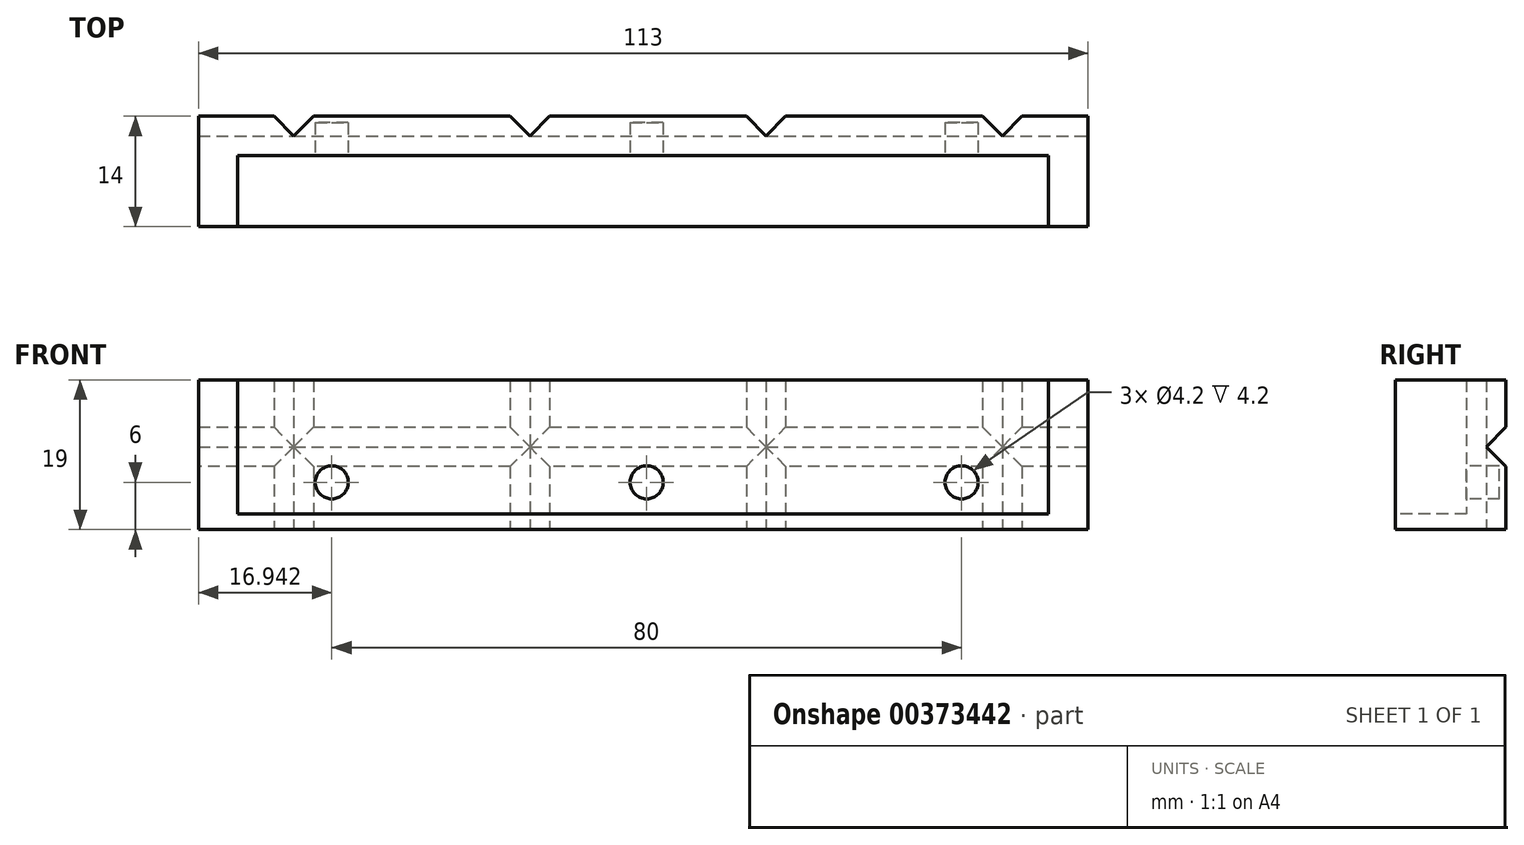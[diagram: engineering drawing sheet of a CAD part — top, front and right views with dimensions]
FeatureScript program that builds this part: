
annotation { "Feature Type Name" : "Feature", "Feature Type Description" : "" }
export const myFeature = defineFeature(function(context is Context, id is Id, definition is map)
    precondition{}
    {
        {
            var Q0;
            Q0=qCreatedBy(makeId("Top.planeOp"),FACE);
            var sketch = newSketch(context, id + "F0", { "sketchPlane" : qUnion([Q0])});
            skLineSegment(sketch, "E0.bottom", {"start": v(-52, -5) * mm, "end": v(51, -5) * mm});
            skLineSegment(sketch, "E0.top", {"start": v(-52, -14) * mm, "end": v(51, -14) * mm});
            skLineSegment(sketch, "E0.left", {"start": v(-52, -5) * mm, "end": v(-52, -14) * mm});
            skLineSegment(sketch, "E0.right", {"start": v(51, -5) * mm, "end": v(51, -14) * mm});
            skLineSegment(sketch, "E1", {"start": v(-57, -14) * mm, "end": v(-57, 0) * mm});
            skLineSegment(sketch, "E2", {"start": v(-57, 0) * mm, "end": v(56, 0) * mm});
            skLineSegment(sketch, "E3", {"start": v(56, 0) * mm, "end": v(56, -14) * mm});
            skLineSegment(sketch, "E4", {"start": v(-52, -14) * mm, "end": v(-57, -14) * mm});
            skLineSegment(sketch, "E5", {"start": v(56, -14) * mm, "end": v(51, -14) * mm});
            skLineSegment(sketch, "E6.direction1", {"start": v(-45, -9.6) * mm, "end": v(-15, -9.6) * mm, "construction": true});
            skLineSegment(sketch, "E7", {"start": v(-48.43, 1.04) * mm, "end": v(-44.9, -2.5) * mm});
            skLineSegment(sketch, "E8", {"start": v(-44.9, -2.5) * mm, "end": v(-41.36, 1.04) * mm});
            skLineSegment(sketch, "E9", {"start": v(-41.36, 1.04) * mm, "end": v(-48.43, 1.04) * mm});
            skLineSegment(sketch, "E10.1.0.0", {"start": v(-11.36, 1.04) * mm, "end": v(-18.43, 1.04) * mm});
            skLineSegment(sketch, "E10.1.0.1", {"start": v(-14.9, -2.5) * mm, "end": v(-11.36, 1.04) * mm});
            skLineSegment(sketch, "E10.1.0.2", {"start": v(-18.43, 1.04) * mm, "end": v(-14.9, -2.5) * mm});
            skLineSegment(sketch, "E10.2.0.0", {"start": v(18.64, 1.04) * mm, "end": v(11.57, 1.04) * mm});
            skLineSegment(sketch, "E10.2.0.1", {"start": v(15.1, -2.5) * mm, "end": v(18.64, 1.04) * mm});
            skLineSegment(sketch, "E10.2.0.2", {"start": v(11.57, 1.04) * mm, "end": v(15.1, -2.5) * mm});
            skLineSegment(sketch, "E10.3.0.0", {"start": v(48.64, 1.04) * mm, "end": v(41.57, 1.04) * mm});
            skLineSegment(sketch, "E10.3.0.1", {"start": v(45.1, -2.5) * mm, "end": v(48.64, 1.04) * mm});
            skLineSegment(sketch, "E10.3.0.2", {"start": v(41.57, 1.04) * mm, "end": v(45.1, -2.5) * mm});
            skLineSegment(sketch, "E10.direction1", {"start": v(-48.43, 1.04) * mm, "end": v(-18.43, 1.04) * mm, "construction": true});
            skSolve(sketch);
        }
        {
            var Q0;
            Q0=makeQuery(id+"F0.imprint","IMPRINT",FACE,{"disambiguationData":[TD([[makeQuery(id+"F0.imprint","IMPRINT",EDGE,{"derivedFrom":sQuery(id+"F0.wireOp",EDGE,"E0.bottom")}),1.0]])]});
            extrude(context, id + "F1", {"entities" : qUnion([Q0]), "depth" : 19 * mm});
        }
        {
            var Q0;
            Q0=makeQuery(id+"F0.imprint","IMPRINT",FACE,{"disambiguationData":[TD([[makeQuery(id+"F0.imprint","IMPRINT",EDGE,{"derivedFrom":sQuery(id+"F0.wireOp",EDGE,"E0.bottom")}),-1.0]])]});
            extrude(context, id + "F2", {"entities" : qUnion([Q0]), "operationType" : NewBodyOperationType.ADD, "depth" : 2 * mm});
        }
        {
            var Q0;
            Q0=makeQuery(id+"F1.opExtrude","SWEPT_FACE",FACE,{"disambiguationData":[OSD([sQuery(id+"F0.wireOp",EDGE,"E3")])]});
            var sketch = newSketch(context, id + "F3", { "sketchPlane" : qUnion([Q0])});
            skLineSegment(sketch, "E11", {"start": v(1.04, 14.04) * mm, "end": v(-2.5, 10.5) * mm});
            skLineSegment(sketch, "E12", {"start": v(-2.5, 10.5) * mm, "end": v(1.04, 6.96) * mm});
            skLineSegment(sketch, "E13", {"start": v(1.04, 14.04) * mm, "end": v(1.04, 6.96) * mm});
            skSolve(sketch);
        }
        {
            var Q0;
            {var subQ0=sQuery(id+"F3.wireOp",EDGE,"E12");var subQ1=sQuery(id+"F3.wireOp",EDGE,"E11");var subQ2=makeQuery(id+"F3.imprint","INTERSECT",VERTEX,{"derivedFrom":[subQ1,subQ0]});Q0=makeQuery(id+"F3.imprint","IMPRINT",FACE,{"disambiguationData":[TD([[makeQuery(id+"F3.imprint","IMPRINT",EDGE,{"disambiguationData":[TD([[subQ2,1.0]])],"derivedFrom":subQ1}),1.0]])]});}
            var Q1;
            {var subQ0=sQuery(id+"F3.wireOp",EDGE,"E13");Q1=makeQuery(id+"F3.imprint","IMPRINT",FACE,{"disambiguationData":[TD([[makeQuery(id+"F3.imprint","IMPRINT",EDGE,{"derivedFrom":subQ0}),-1.0]])]});}
            extrude(context, id + "F4", {"entities" : qUnion([Q0, Q1]), "operationType" : NewBodyOperationType.REMOVE, "oppositeDirection" : true, "depth" : 120 * mm});
        }
        {
            var Q0;
            Q0=makeQuery(id+"F1.opExtrude","SWEPT_FACE",FACE,{"disambiguationData":[OSD([sQuery(id+"F0.wireOp",EDGE,"E0.bottom")])]});
            var sketch = newSketch(context, id + "F5", { "sketchPlane" : qUnion([Q0])});
            skCircle(sketch, "E14", {"center": v(-40.06, 6) * mm, "radius": 2.1 * mm});
            skCircle(sketch, "E15.1.0.0", {"center": v(-0.06, 6) * mm, "radius": 2.1 * mm});
            skCircle(sketch, "E15.2.0.0", {"center": v(39.94, 6) * mm, "radius": 2.1 * mm});
            skLineSegment(sketch, "E15.direction1", {"start": v(-40.06, 6) * mm, "end": v(-0.06, 6) * mm, "construction": true});
            skSolve(sketch);
        }
        {
            var Q0;
            Q0=makeQuery(id+"F5.imprint","IMPRINT",FACE,{"disambiguationData":[TD([[makeQuery(id+"F5.imprint","IMPRINT",EDGE,{"derivedFrom":sQuery(id+"F5.wireOp",EDGE,"E14")}),1.0]])]});
            var Q1;
            Q1=makeQuery(id+"F5.imprint","IMPRINT",FACE,{"disambiguationData":[TD([[makeQuery(id+"F5.imprint","IMPRINT",EDGE,{"derivedFrom":sQuery(id+"F5.wireOp",EDGE,"E15.1.0.0")}),1.0]])]});
            var Q2;
            Q2=makeQuery(id+"F5.imprint","IMPRINT",FACE,{"disambiguationData":[TD([[makeQuery(id+"F5.imprint","IMPRINT",EDGE,{"derivedFrom":sQuery(id+"F5.wireOp",EDGE,"E15.2.0.0")}),1.0]])]});
            extrude(context, id + "F6", {"entities" : qUnion([Q0, Q1, Q2]), "operationType" : NewBodyOperationType.REMOVE, "oppositeDirection" : true, "depth" : 4.2 * mm});
        }
    });
